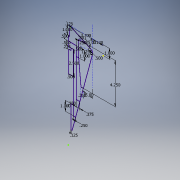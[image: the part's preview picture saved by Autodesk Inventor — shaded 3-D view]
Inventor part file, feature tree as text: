
AUTODESK INVENTOR PART (.ipt)
format: ipt  version: 2017 (Build 210142000, 142)  size: 125,440 bytes
history: native  units: in
note: dims shown in document units (in); Inventor stores cm internally (conversion verified against a paired STEP export)
features: sketch x1
ambient origin geometry x8: Origin, YZ Plane, XZ Plane, XY Plane, X Axis, Y Axis, Z Axis, Center Point
feature tree (1):
  sketch  "Sketch1"  dims[d0=1.13in d1=3.7in d2=0.125in d3=0.1718in d5=1.0in d6=1.0in d7=90.0deg d8=0.5in d9=15.0deg d12=1.25in d13=0.25in d16=0.5in d17=0.5in d18=0.5in d19=2.5in d20=0.5in d22=0.375in d23=0.25in d25=0.234in d27=0.125in d28=0.25in d29=1.0in d30=4.25in d31=0.25in d32=1.0in d33=0.8014in d34=15.0deg]
